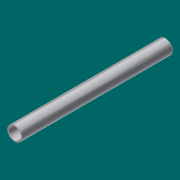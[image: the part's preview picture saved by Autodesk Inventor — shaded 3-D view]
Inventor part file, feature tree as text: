
AUTODESK INVENTOR PART (.ipt)
format: ipt  version: 2017 (Build 210142000, 142)  size: 117,760 bytes
history: native  units: in
note: dims shown in document units (in); Inventor stores cm internally (conversion verified against a paired STEP export)
features: extrude x1, sketch x1
ambient origin geometry x8: Origin, YZ Plane, XZ Plane, XY Plane, X Axis, Y Axis, Z Axis, Center Point
bodies: Solid1 (feature_tree)
feature tree (2):
  extrude  "Extrusion1"  Depth=30.25in
  sketch  "Sketch1"  dims[d0=2.875in d1=2.469in d2=30.25in d3=0.0in]
